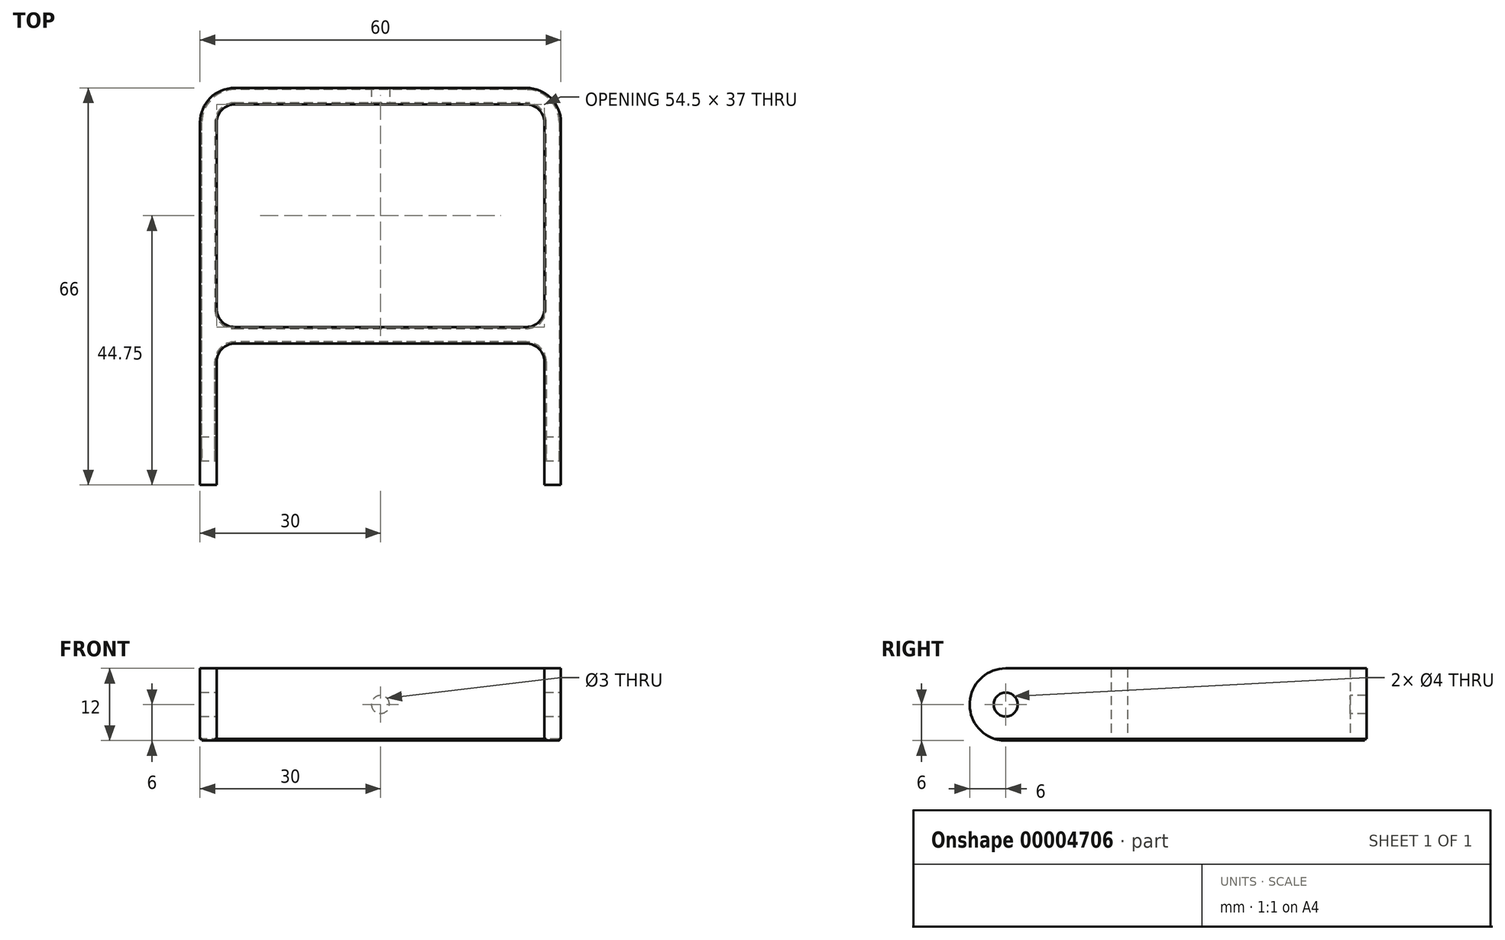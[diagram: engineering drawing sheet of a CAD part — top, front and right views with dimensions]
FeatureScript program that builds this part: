
annotation { "Feature Type Name" : "Feature", "Feature Type Description" : "" }
export const myFeature = defineFeature(function(context is Context, id is Id, definition is map)
    precondition{}
    {
        {
            var Q0;
            Q0=qCreatedBy(makeId("Top.planeOp"),FACE);
            var sketch = newSketch(context, id + "F0", { "sketchPlane" : qUnion([Q0])});
            skLineSegment(sketch, "E0", {"start": v(0, 0) * mm, "end": v(0, 63.25) * mm, "construction": true});
            skLineSegment(sketch, "E1", {"start": v(-27.25, 63.25) * mm, "end": v(27.25, 63.25) * mm});
            skLineSegment(sketch, "E2", {"start": v(27.25, 0) * mm, "end": v(30, 0) * mm});
            skLineSegment(sketch, "E3", {"start": v(30, 0) * mm, "end": v(30, 66) * mm});
            skLineSegment(sketch, "E4", {"start": v(30, 66) * mm, "end": v(-30, 66) * mm});
            skLineSegment(sketch, "E5", {"start": v(-30, 66) * mm, "end": v(-30, 0) * mm});
            skLineSegment(sketch, "E6", {"start": v(-30, 0) * mm, "end": v(-27.25, 0) * mm});
            skLineSegment(sketch, "E7", {"start": v(-27.25, 63.25) * mm, "end": v(-27.25, 26.25) * mm});
            skLineSegment(sketch, "E8", {"start": v(-27.25, 26.25) * mm, "end": v(27.25, 26.25) * mm});
            skLineSegment(sketch, "E9", {"start": v(27.25, 26.25) * mm, "end": v(27.25, 63.25) * mm});
            skLineSegment(sketch, "E10", {"start": v(27.25, 0) * mm, "end": v(27.25, 23.5) * mm});
            skLineSegment(sketch, "E11", {"start": v(27.25, 23.5) * mm, "end": v(-27.25, 23.5) * mm});
            skLineSegment(sketch, "E12", {"start": v(-27.25, 23.5) * mm, "end": v(-27.25, 0) * mm});
            skLineSegment(sketch, "E13", {"start": v(-27.25, 26.25) * mm, "end": v(-27.25, 23.5) * mm, "construction": true});
            skLineSegment(sketch, "E14", {"start": v(-27.25, 26.25) * mm, "end": v(-30, 26.25) * mm, "construction": true});
            skLineSegment(sketch, "E15", {"start": v(-27.25, 63.25) * mm, "end": v(-27.25, 66) * mm, "construction": true});
            skSolve(sketch);
        }
        {
            var Q0;
            Q0 = qSketchRegion(id + "F0", true);
            extrude(context, id + "F1", {"entities" : qUnion([Q0]), "depth" : 12 * mm});
        }
        {
            var Q0;
            Q0=makeQuery(id+"F1.opExtrude","CAP_EDGE",EDGE,{"disambiguationData":[OSD([sQuery(id+"F0.wireOp",EDGE,"E6")])],"isStart":false});
            var Q1;
            Q1=makeQuery(id+"F1.opExtrude","CAP_EDGE",EDGE,{"disambiguationData":[OSD([sQuery(id+"F0.wireOp",EDGE,"E6")])],"isStart":true});
            var Q2;
            Q2=makeQuery(id+"F1.opExtrude","CAP_EDGE",EDGE,{"disambiguationData":[OSD([sQuery(id+"F0.wireOp",EDGE,"E2")])],"isStart":false});
            var Q3;
            Q3=makeQuery(id+"F1.opExtrude","CAP_EDGE",EDGE,{"disambiguationData":[OSD([sQuery(id+"F0.wireOp",EDGE,"E2")])],"isStart":true});
            fillet(context, id + "F2", {"entities" : qUnion([Q0, Q1, Q2, Q3]), "radius" : 6 * mm, "tangentPropagation" : true, "allowEdgeOverflow" : false});
        }
        {
            var Q0;
            Q0=makeQuery(id+"F1.opExtrude","SWEPT_FACE",FACE,{"disambiguationData":[OSD([sQuery(id+"F0.wireOp",EDGE,"E3")])]});
            var sketch = newSketch(context, id + "F3", { "sketchPlane" : qUnion([Q0])});
            skCircle(sketch, "E16", {"center": v(6, 6) * mm, "radius": 2 * mm});
            skSolve(sketch);
        }
        {
            var Q0;
            Q0 = qSketchRegion(id + "F3", true);
            extrude(context, id + "F4", {"entities" : qUnion([Q0]), "operationType" : NewBodyOperationType.REMOVE, "endBound" : BoundingType.THROUGH_ALL, "oppositeDirection" : true, "depth" : 25 * mm});
        }
        {
            var Q0;
            Q0=makeQuery(id+"F1.opExtrude","SWEPT_FACE",FACE,{"disambiguationData":[OSD([sQuery(id+"F0.wireOp",EDGE,"E1")])]});
            var sketch = newSketch(context, id + "F5", { "sketchPlane" : qUnion([Q0])});
            skLineSegment(sketch, "E17", {"start": v(0, 12) * mm, "end": v(0, 0) * mm, "construction": true});
            skCircle(sketch, "E18", {"center": v(0, 6) * mm, "radius": 1.5 * mm});
            skSolve(sketch);
        }
        {
            var Q0;
            Q0 = qSketchRegion(id + "F5", true);
            var Q1;
            Q1=makeQuery(id+"F1.opExtrude","SWEPT_FACE",FACE,{"disambiguationData":[OSD([sQuery(id+"F0.wireOp",EDGE,"E4")])]});
            extrude(context, id + "F6", {"entities" : qUnion([Q0]), "operationType" : NewBodyOperationType.REMOVE, "endBound" : BoundingType.UP_TO_SURFACE, "oppositeDirection" : true, "endBoundEntityFace" : qUnion([Q1]), "depth" : 25 * mm});
        }
        {
            var Q0;
            Q0=makeQuery(id+"F1.opExtrude","SWEPT_EDGE",EDGE,{"disambiguationData":[OSD([sQuery(id+"F0.wireOp",EDGE,"E1"),sQuery(id+"F0.wireOp",EDGE,"E7")])]});
            var Q1;
            Q1=makeQuery(id+"F1.opExtrude","SWEPT_EDGE",EDGE,{"disambiguationData":[OSD([sQuery(id+"F0.wireOp",EDGE,"E11"),sQuery(id+"F0.wireOp",EDGE,"E12")])]});
            var Q2;
            Q2=makeQuery(id+"F1.opExtrude","SWEPT_EDGE",EDGE,{"disambiguationData":[OSD([sQuery(id+"F0.wireOp",EDGE,"E7"),sQuery(id+"F0.wireOp",EDGE,"E8")])]});
            var Q3;
            Q3=makeQuery(id+"F1.opExtrude","SWEPT_EDGE",EDGE,{"disambiguationData":[OSD([sQuery(id+"F0.wireOp",EDGE,"E1"),sQuery(id+"F0.wireOp",EDGE,"E9")])]});
            var Q4;
            Q4=makeQuery(id+"F1.opExtrude","SWEPT_EDGE",EDGE,{"disambiguationData":[OSD([sQuery(id+"F0.wireOp",EDGE,"E10"),sQuery(id+"F0.wireOp",EDGE,"E11")])]});
            var Q5;
            Q5=makeQuery(id+"F1.opExtrude","SWEPT_EDGE",EDGE,{"disambiguationData":[OSD([sQuery(id+"F0.wireOp",EDGE,"E8"),sQuery(id+"F0.wireOp",EDGE,"E9")])]});
            fillet(context, id + "F7", {"entities" : qUnion([Q0, Q1, Q2, Q3, Q4, Q5]), "radius" : 3 * mm, "tangentPropagation" : true, "allowEdgeOverflow" : false});
        }
        {
            var Q0;
            Q0=makeQuery(id+"F1.opExtrude","SWEPT_EDGE",EDGE,{"disambiguationData":[OSD([sQuery(id+"F0.wireOp",EDGE,"E4"),sQuery(id+"F0.wireOp",EDGE,"E5")])]});
            var Q1;
            Q1=makeQuery(id+"F1.opExtrude","SWEPT_EDGE",EDGE,{"disambiguationData":[OSD([sQuery(id+"F0.wireOp",EDGE,"E3"),sQuery(id+"F0.wireOp",EDGE,"E4")])]});
            fillet(context, id + "F8", {"entities" : qUnion([Q0, Q1]), "radius" : 5.75 * mm, "tangentPropagation" : true, "allowEdgeOverflow" : false});
        }
        {
            var Q0;
            Q0=makeQuery(id+"F1.opExtrude","CAP_FACE",FACE,{"disambiguationData":[OSD([sQuery(id+"F0.wireOp",EDGE,"E1"),sQuery(id+"F0.wireOp",EDGE,"E2"),sQuery(id+"F0.wireOp",EDGE,"E3"),sQuery(id+"F0.wireOp",EDGE,"E4"),sQuery(id+"F0.wireOp",EDGE,"E5"),sQuery(id+"F0.wireOp",EDGE,"E6"),sQuery(id+"F0.wireOp",EDGE,"E7"),sQuery(id+"F0.wireOp",EDGE,"E8"),sQuery(id+"F0.wireOp",EDGE,"E9"),sQuery(id+"F0.wireOp",EDGE,"E10"),sQuery(id+"F0.wireOp",EDGE,"E11"),sQuery(id+"F0.wireOp",EDGE,"E12")])],"isStart":true});
            var sketch = newSketch(context, id + "F9", { "sketchPlane" : qUnion([Q0])});
            skLineSegment(sketch, "E19.0", {"start": v(30, -6) * mm, "end": v(30, -60.25) * mm});
            skArc(sketch, "E19.1", {"start": v(24.25, -66) * mm, "mid": v(28.32, -64.32) * mm, "end": v(30, -60.25) * mm});
            skLineSegment(sketch, "E19.3", {"start": v(24.25, -66) * mm, "end": v(-24.25, -66) * mm});
            skArc(sketch, "E19.8", {"start": v(27.25, -20.5) * mm, "mid": v(26.37, -22.62) * mm, "end": v(24.25, -23.5) * mm});
            skLineSegment(sketch, "E19.9", {"start": v(27.25, -6) * mm, "end": v(27.25, -20.5) * mm});
            skLineSegment(sketch, "E19.10", {"start": v(24.25, -23.5) * mm, "end": v(-24.25, -23.5) * mm});
            skArc(sketch, "E19.11", {"start": v(-24.25, -23.5) * mm, "mid": v(-26.37, -22.62) * mm, "end": v(-27.25, -20.5) * mm});
            skLineSegment(sketch, "E19.12", {"start": v(-27.25, -20.5) * mm, "end": v(-27.25, -6) * mm});
            skLineSegment(sketch, "E19.13", {"start": v(-30, -60.25) * mm, "end": v(-30, -6) * mm});
            skArc(sketch, "E19.17", {"start": v(-30, -60.25) * mm, "mid": v(-28.32, -64.32) * mm, "end": v(-24.25, -66) * mm});
            skLineSegment(sketch, "E20.0", {"start": v(27.25, -6) * mm, "end": v(27.25, 0) * mm});
            skLineSegment(sketch, "E21.0", {"start": v(30, -6) * mm, "end": v(30, 0) * mm});
            skLineSegment(sketch, "E22.0", {"start": v(-30, 0) * mm, "end": v(-30, -6) * mm});
            skLineSegment(sketch, "E22.1", {"start": v(-27.25, 0) * mm, "end": v(-27.25, -6) * mm});
            skLineSegment(sketch, "E23.0", {"start": v(27.55, -6) * mm, "end": v(27.55, 0) * mm});
            skLineSegment(sketch, "E23.1", {"start": v(27.55, -6) * mm, "end": v(27.55, -20.5) * mm});
            skArc(sketch, "E23.2", {"start": v(27.55, -20.5) * mm, "mid": v(26.58, -22.83) * mm, "end": v(24.25, -23.8) * mm});
            skLineSegment(sketch, "E23.3", {"start": v(24.25, -23.8) * mm, "end": v(-24.25, -23.8) * mm});
            skArc(sketch, "E23.4", {"start": v(-24.25, -23.8) * mm, "mid": v(-26.58, -22.83) * mm, "end": v(-27.55, -20.5) * mm});
            skLineSegment(sketch, "E23.5", {"start": v(-27.55, -20.5) * mm, "end": v(-27.55, -6) * mm});
            skLineSegment(sketch, "E23.6", {"start": v(-27.55, 0) * mm, "end": v(-27.55, -6) * mm});
            skLineSegment(sketch, "E24", {"start": v(-27.55, 0) * mm, "end": v(-27.25, 0) * mm});
            skLineSegment(sketch, "E25", {"start": v(27.55, 0) * mm, "end": v(27.25, 0) * mm});
            skLineSegment(sketch, "E26.0", {"start": v(29.7, -6) * mm, "end": v(29.7, 0) * mm});
            skLineSegment(sketch, "E26.1", {"start": v(29.7, -6) * mm, "end": v(29.7, -60.25) * mm});
            skArc(sketch, "E26.2", {"start": v(24.25, -65.7) * mm, "mid": v(28.1, -64.1) * mm, "end": v(29.7, -60.25) * mm});
            skLineSegment(sketch, "E26.3", {"start": v(24.25, -65.7) * mm, "end": v(-24.25, -65.7) * mm});
            skArc(sketch, "E26.4", {"start": v(-29.7, -60.25) * mm, "mid": v(-28.1, -64.1) * mm, "end": v(-24.25, -65.7) * mm});
            skLineSegment(sketch, "E26.5", {"start": v(-29.7, -60.25) * mm, "end": v(-29.7, -6) * mm});
            skLineSegment(sketch, "E26.6", {"start": v(-29.7, 0) * mm, "end": v(-29.7, -6) * mm});
            skLineSegment(sketch, "E27", {"start": v(30, 0) * mm, "end": v(29.7, 0) * mm});
            skLineSegment(sketch, "E28", {"start": v(-29.7, 0) * mm, "end": v(-30, 0) * mm});
            skSolve(sketch);
        }
        {
            var Q0;
            Q0 = qSketchRegion(id + "F9", true);
            extrude(context, id + "F10", {"entities" : qUnion([Q0]), "operationType" : NewBodyOperationType.REMOVE, "oppositeDirection" : true, "depth" : 0.3 * mm});
        }
        {
            var Q0;
            Q0=makeQuery(id+"F1.opExtrude","CAP_FACE",FACE,{"disambiguationData":[OSD([sQuery(id+"F0.wireOp",EDGE,"E1"),sQuery(id+"F0.wireOp",EDGE,"E2"),sQuery(id+"F0.wireOp",EDGE,"E3"),sQuery(id+"F0.wireOp",EDGE,"E4"),sQuery(id+"F0.wireOp",EDGE,"E5"),sQuery(id+"F0.wireOp",EDGE,"E6"),sQuery(id+"F0.wireOp",EDGE,"E7"),sQuery(id+"F0.wireOp",EDGE,"E8"),sQuery(id+"F0.wireOp",EDGE,"E9"),sQuery(id+"F0.wireOp",EDGE,"E10"),sQuery(id+"F0.wireOp",EDGE,"E11"),sQuery(id+"F0.wireOp",EDGE,"E12")])],"isStart":true});
            var sketch = newSketch(context, id + "F11", { "sketchPlane" : qUnion([Q0])});
            skArc(sketch, "E29.0", {"start": v(24.25, -26.25) * mm, "mid": v(26.37, -27.13) * mm, "end": v(27.25, -29.25) * mm});
            skLineSegment(sketch, "E29.1", {"start": v(27.25, -29.25) * mm, "end": v(27.25, -60.25) * mm});
            skArc(sketch, "E29.2", {"start": v(27.25, -60.25) * mm, "mid": v(26.37, -62.37) * mm, "end": v(24.25, -63.25) * mm});
            skLineSegment(sketch, "E29.3", {"start": v(-24.25, -63.25) * mm, "end": v(24.25, -63.25) * mm});
            skArc(sketch, "E29.4", {"start": v(-24.25, -63.25) * mm, "mid": v(-26.37, -62.37) * mm, "end": v(-27.25, -60.25) * mm});
            skLineSegment(sketch, "E29.5", {"start": v(-27.25, -60.25) * mm, "end": v(-27.25, -29.25) * mm});
            skArc(sketch, "E29.6", {"start": v(-27.25, -29.25) * mm, "mid": v(-26.37, -27.13) * mm, "end": v(-24.25, -26.25) * mm});
            skLineSegment(sketch, "E29.7", {"start": v(-24.25, -26.25) * mm, "end": v(24.25, -26.25) * mm});
            skArc(sketch, "E30.0", {"start": v(-27.55, -29.25) * mm, "mid": v(-26.58, -26.92) * mm, "end": v(-24.25, -25.95) * mm});
            skLineSegment(sketch, "E30.1", {"start": v(-27.55, -60.25) * mm, "end": v(-27.55, -29.25) * mm});
            skArc(sketch, "E30.2", {"start": v(-24.25, -63.55) * mm, "mid": v(-26.58, -62.58) * mm, "end": v(-27.55, -60.25) * mm});
            skLineSegment(sketch, "E30.3", {"start": v(-24.25, -63.55) * mm, "end": v(24.25, -63.55) * mm});
            skArc(sketch, "E30.4", {"start": v(27.55, -60.25) * mm, "mid": v(26.58, -62.58) * mm, "end": v(24.25, -63.55) * mm});
            skLineSegment(sketch, "E30.5", {"start": v(-24.25, -25.95) * mm, "end": v(24.25, -25.95) * mm});
            skLineSegment(sketch, "E30.6", {"start": v(27.55, -29.25) * mm, "end": v(27.55, -60.25) * mm});
            skArc(sketch, "E30.7", {"start": v(24.25, -25.95) * mm, "mid": v(26.58, -26.92) * mm, "end": v(27.55, -29.25) * mm});
            skSolve(sketch);
        }
        {
            var Q0;
            Q0 = qSketchRegion(id + "F11", true);
            extrude(context, id + "F12", {"entities" : qUnion([Q0]), "operationType" : NewBodyOperationType.REMOVE, "oppositeDirection" : true, "depth" : 0.3 * mm});
        }
    });
